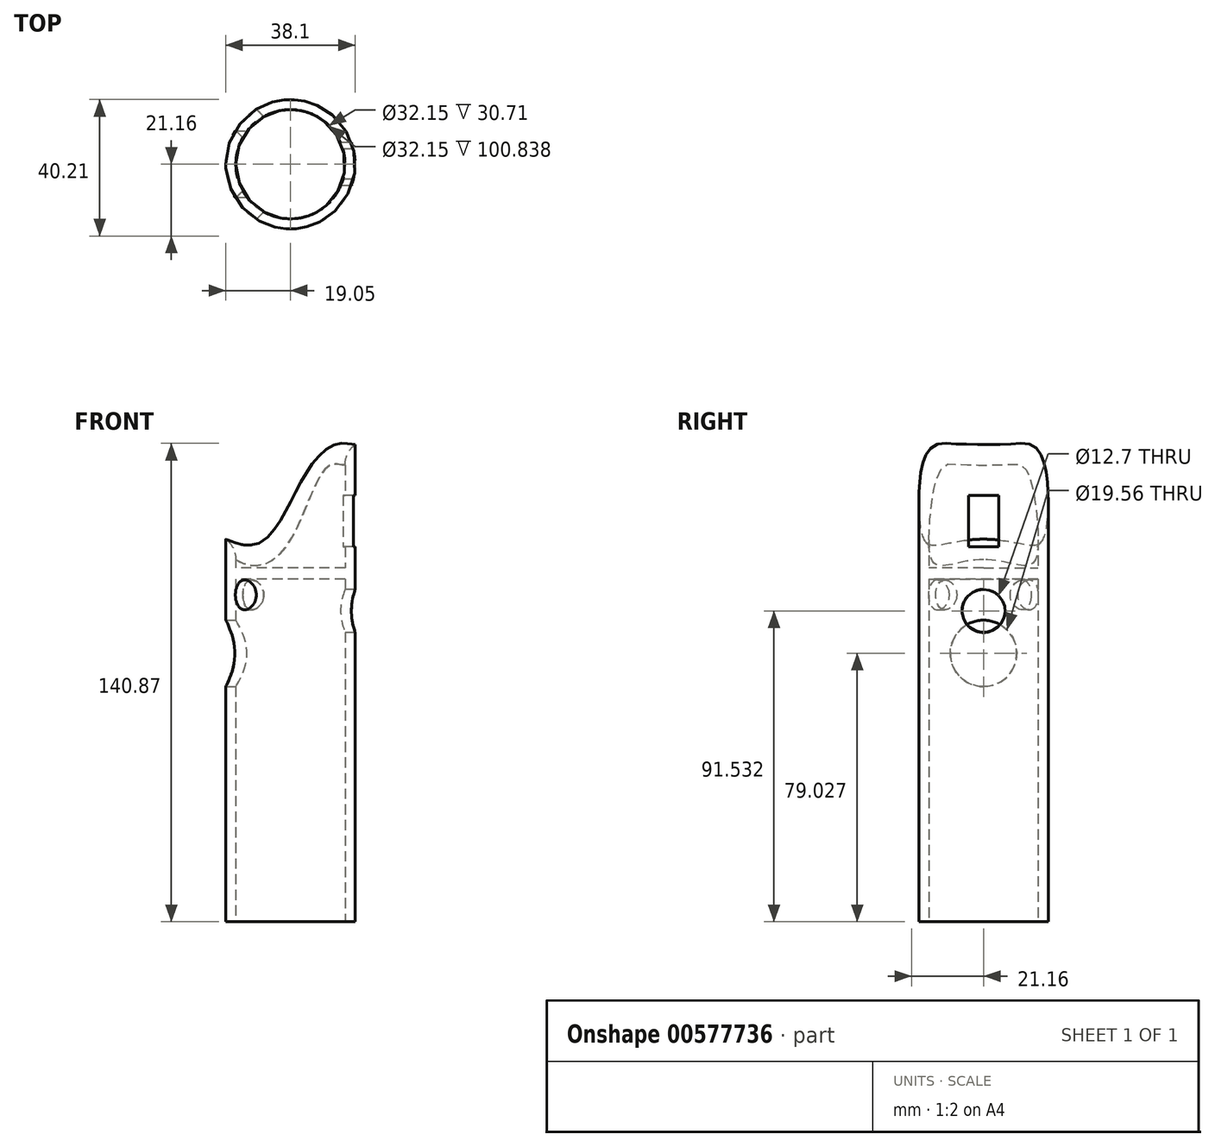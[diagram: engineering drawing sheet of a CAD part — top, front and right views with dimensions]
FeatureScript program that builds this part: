
annotation { "Feature Type Name" : "Feature", "Feature Type Description" : "" }
export const myFeature = defineFeature(function(context is Context, id is Id, definition is map)
    precondition{}
    {
        {
            var Q0;
            Q0=qCreatedBy(makeId("Top.planeOp"),FACE);
            var sketch = newSketch(context, id + "F0", { "sketchPlane" : qUnion([Q0])});
            skCircle(sketch, "E0", {"center": v(0, 0) * mm, "radius": 19.05 * mm});
            skSolve(sketch);
        }
        {
            var Q0;
            Q0=makeQuery(id+"F0.imprint","IMPRINT",FACE,{"disambiguationData":[TD([[makeQuery(id+"F0.imprint","IMPRINT",EDGE,{"derivedFrom":sQuery(id+"F0.wireOp",EDGE,"E0")}),1.0]])]});
            extrude(context, id + "F1", {"entities" : qUnion([Q0]), "depth" : 150.88 * mm, "offsetDistance" : 25.4 * mm});
        }
        {
            var Q0;
            Q0=qCreatedBy(makeId("Top.planeOp"),FACE);
            var sketch = newSketch(context, id + "F2", { "sketchPlane" : qUnion([Q0])});
            skCircle(sketch, "E1", {"center": v(0, 0) * mm, "radius": 16.08 * mm});
            skSolve(sketch);
        }
        {
            var Q0;
            Q0=makeQuery(id+"F2.imprint","IMPRINT",FACE,{"disambiguationData":[TD([[makeQuery(id+"F2.imprint","IMPRINT",EDGE,{"derivedFrom":sQuery(id+"F2.wireOp",EDGE,"E1")}),1.0]])]});
            extrude(context, id + "F3", {"entities" : qUnion([Q0]), "operationType" : NewBodyOperationType.REMOVE, "depth" : 268.48 * mm, "offsetDistance" : 25.4 * mm});
        }
        {
            var Q0;
            Q0=qCreatedBy(makeId("Front.planeOp"),FACE);
            var sketch = newSketch(context, id + "F4", { "sketchPlane" : qUnion([Q0])});
            skFitSpline(sketch, "E2", {"points": [v(-21.66, 122.68) * mm, v(21.18, 150.93) * mm], "startDerivative": vector(64.98, -30.37) * mm, "endDerivative": vector(63.54, -9.4) * mm});
            skLineSegment(sketch, "E3", {"start": v(-21.66, 122.68) * mm, "end": v(-21.66, 155.89) * mm});
            skLineSegment(sketch, "E4", {"start": v(-21.66, 155.89) * mm, "end": v(21.18, 150.93) * mm});
            skSolve(sketch);
        }
        {
            var Q0;
            {var subQ0=sQuery(id+"F4.wireOp",EDGE,"E3");Q0=makeQuery(id+"F4.imprint","IMPRINT",FACE,{"disambiguationData":[TD([[makeQuery(id+"F4.imprint","IMPRINT",EDGE,{"derivedFrom":subQ0}),-1.0]])]});}
            extrude(context, id + "F5", {"entities" : qUnion([Q0]), "operationType" : NewBodyOperationType.REMOVE, "oppositeDirection" : true, "depth" : 35.05 * mm, "offsetDistance" : 25.4 * mm});
        }
        {
            var Q0;
            {var subQ0=sQuery(id+"F4.wireOp",EDGE,"E3");Q0=makeQuery(id+"F4.imprint","IMPRINT",FACE,{"disambiguationData":[TD([[makeQuery(id+"F4.imprint","IMPRINT",EDGE,{"derivedFrom":subQ0}),-1.0]])]});}
            extrude(context, id + "F6", {"entities" : qUnion([Q0]), "operationType" : NewBodyOperationType.REMOVE, "depth" : 66.3 * mm, "offsetDistance" : 25.4 * mm});
        }
        {
            var Q0;
            Q0=makeQuery(id+"F6.boolean.opBoolean","INTERSECT",EDGE,{"derivedFrom":[makeQuery(id+"F3.boolean.opBoolean","COPY",FACE,{"derivedFrom":makeQuery(id+"F3.opExtrude","SWEPT_FACE",FACE,{"disambiguationData":[OSD([sQuery(id+"F2.wireOp",EDGE,"E1")])]})}),makeQuery(id+"F6.opExtrude","SWEPT_FACE",FACE,{"disambiguationData":[OSD([sQuery(id+"F4.wireOp",EDGE,"E2")])]})]});
            fillet(context, id + "F7", {"entities" : qUnion([Q0]), "radius" : 7.62 * mm, "tangentPropagation" : true, "allowEdgeOverflow" : false});
        }
        {
            var Q0;
            Q0=qCreatedBy(makeId("Top.planeOp"),FACE);
            var sketch = newSketch(context, id + "F8", { "sketchPlane" : qUnion([Q0])});
            skCircle(sketch, "E5", {"center": v(0, 0) * mm, "radius": 39.13 * mm});
            skSolve(sketch);
        }
        {
            var Q0;
            Q0=makeQuery(id+"F8.imprint","IMPRINT",FACE,{"disambiguationData":[TD([[makeQuery(id+"F8.imprint","IMPRINT",EDGE,{"derivedFrom":sQuery(id+"F8.wireOp",EDGE,"E5")}),1.0]])]});
            extrude(context, id + "F9", {"entities" : qUnion([Q0]), "operationType" : NewBodyOperationType.REMOVE, "depth" : 8.64 * mm, "offsetDistance" : 25.4 * mm});
        }
        {
            var Q0;
            Q0=qCreatedBy(makeId("Right.planeOp"),FACE);
            var sketch = newSketch(context, id + "F10", { "sketchPlane" : qUnion([Q0])});
            skCircle(sketch, "E6", {"center": v(0, 100.17) * mm, "radius": 6.35 * mm});
            skSolve(sketch);
        }
        {
            var Q0;
            Q0=makeQuery(id+"F10.imprint","IMPRINT",FACE,{"disambiguationData":[TD([[makeQuery(id+"F10.imprint","IMPRINT",EDGE,{"derivedFrom":sQuery(id+"F10.wireOp",EDGE,"E6")}),1.0]])]});
            extrude(context, id + "F11", {"entities" : qUnion([Q0]), "operationType" : NewBodyOperationType.REMOVE, "depth" : 66.8 * mm, "offsetDistance" : 25.4 * mm});
        }
        {
            var Q0;
            Q0=qCreatedBy(makeId("Right.planeOp"),FACE);
            var sketch = newSketch(context, id + "F12", { "sketchPlane" : qUnion([Q0])});
            skCircle(sketch, "E7", {"center": v(0, 87.67) * mm, "radius": 9.78 * mm});
            skSolve(sketch);
        }
        {
            var Q0;
            Q0=makeQuery(id+"F12.imprint","IMPRINT",FACE,{"disambiguationData":[TD([[makeQuery(id+"F12.imprint","IMPRINT",EDGE,{"derivedFrom":sQuery(id+"F12.wireOp",EDGE,"E7")}),1.0]])]});
            extrude(context, id + "F13", {"entities" : qUnion([Q0]), "operationType" : NewBodyOperationType.REMOVE, "oppositeDirection" : true, "depth" : 36.07 * mm, "offsetDistance" : 25.4 * mm});
        }
        {
            var Q0;
            Q0=qCreatedBy(makeId("Right.planeOp"),FACE);
            var sketch = newSketch(context, id + "F14", { "sketchPlane" : qUnion([Q0])});
            skLineSegment(sketch, "E8.bottom", {"start": v(4.45, 119) * mm, "end": v(-4.44, 119) * mm});
            skLineSegment(sketch, "E8.top", {"start": v(4.45, 134.17) * mm, "end": v(-4.44, 134.17) * mm});
            skLineSegment(sketch, "E8.left", {"start": v(4.44, 119) * mm, "end": v(4.45, 134.17) * mm});
            skLineSegment(sketch, "E8.right", {"start": v(-4.45, 119) * mm, "end": v(-4.44, 134.17) * mm});
            skPoint(sketch, "E8.middle", {"position": v(0, 126.59) * mm});
            skSolve(sketch);
        }
        {
            var Q0;
            Q0=makeQuery(id+"F14.imprint","IMPRINT",FACE,{"disambiguationData":[TD([[makeQuery(id+"F14.imprint","IMPRINT",EDGE,{"derivedFrom":sQuery(id+"F14.wireOp",EDGE,"E8.bottom")}),-1.0]])]});
            extrude(context, id + "F15", {"entities" : qUnion([Q0]), "operationType" : NewBodyOperationType.REMOVE, "depth" : 49.78 * mm, "offsetDistance" : 25.4 * mm});
        }
        {
            var Q0;
            Q0=qCreatedBy(makeId("Right.planeOp"),FACE);
            var Q1;
            Q1=qCreatedBy(makeId("Front.planeOp"),FACE);
            cPlane(context, id + "F16", {"entities" : qUnion([Q0, Q1]), "cplaneType" : CPlaneType.MID_PLANE, "offset" : 25.4 * mm, "width" : 152.4 * mm, "height" : 152.4 * mm});
        }
        {
            var Q0;
            Q0=qCreatedBy(makeId("Right.planeOp"),FACE);
            var Q1;
            Q1=qCreatedBy(makeId("Front.planeOp"),FACE);
            cPlane(context, id + "F17", {"entities" : qUnion([Q0, Q1]), "cplaneType" : CPlaneType.MID_PLANE, "offset" : 25.4 * mm, "flipAlignment" : true, "width" : 152.4 * mm, "height" : 152.4 * mm});
        }
        {
            var Q0;
            Q0=qCreatedBy(id+"F16.planeOp",FACE);
            var sketch = newSketch(context, id + "F18", { "sketchPlane" : qUnion([Q0])});
            skCircle(sketch, "E9", {"center": v(0, 104.88) * mm, "radius": 4.37 * mm});
            skLineSegment(sketch, "E10", {"start": v(0, 104.88) * mm, "end": v(0, 0) * mm});
            skSolve(sketch);
        }
        {
            var Q0;
            Q0=makeQuery(id+"F18.imprint","IMPRINT",FACE,{"disambiguationData":[TD([[makeQuery(id+"F18.imprint","IMPRINT",EDGE,{"derivedFrom":sQuery(id+"F18.wireOp",EDGE,"E9")}),1.0]])]});
            extrude(context, id + "F19", {"entities" : qUnion([Q0]), "operationType" : NewBodyOperationType.REMOVE, "oppositeDirection" : true, "depth" : 27.43 * mm, "offsetDistance" : 25.4 * mm});
        }
        {
            var Q0;
            Q0=qCreatedBy(id+"F17.planeOp",FACE);
            var sketch = newSketch(context, id + "F20", { "sketchPlane" : qUnion([Q0])});
            skCircle(sketch, "E11", {"center": v(0, 104.88) * mm, "radius": 4.37 * mm});
            skLineSegment(sketch, "E12", {"start": v(0, 104.88) * mm, "end": v(0, 0) * mm});
            skSolve(sketch);
        }
        {
            var Q0;
            Q0=makeQuery(id+"F20.imprint","IMPRINT",FACE,{"disambiguationData":[TD([[makeQuery(id+"F20.imprint","IMPRINT",EDGE,{"derivedFrom":sQuery(id+"F20.wireOp",EDGE,"E11")}),1.0]])]});
            extrude(context, id + "F21", {"entities" : qUnion([Q0]), "operationType" : NewBodyOperationType.REMOVE, "oppositeDirection" : true, "depth" : 31.24 * mm, "offsetDistance" : 25.4 * mm});
        }
        {
            var Q0;
            Q0=makeQuery(id+"F2.imprint","IMPRINT",FACE,{"disambiguationData":[TD([[makeQuery(id+"F2.imprint","IMPRINT",EDGE,{"derivedFrom":sQuery(id+"F2.wireOp",EDGE,"E1")}),1.0]])]});
            extrude(context, id + "F22", {"entities" : qUnion([Q0]), "operationType" : NewBodyOperationType.ADD, "depth" : 112.78 * mm, "offsetDistance" : 25.4 * mm});
        }
        {
            var Q0;
            Q0 = qSketchRegion(id + "F2", true);
            extrude(context, id + "F23", {"entities" : qUnion([Q0]), "operationType" : NewBodyOperationType.REMOVE, "depth" : 109.47 * mm, "offsetDistance" : 25.4 * mm});
        }
    });
